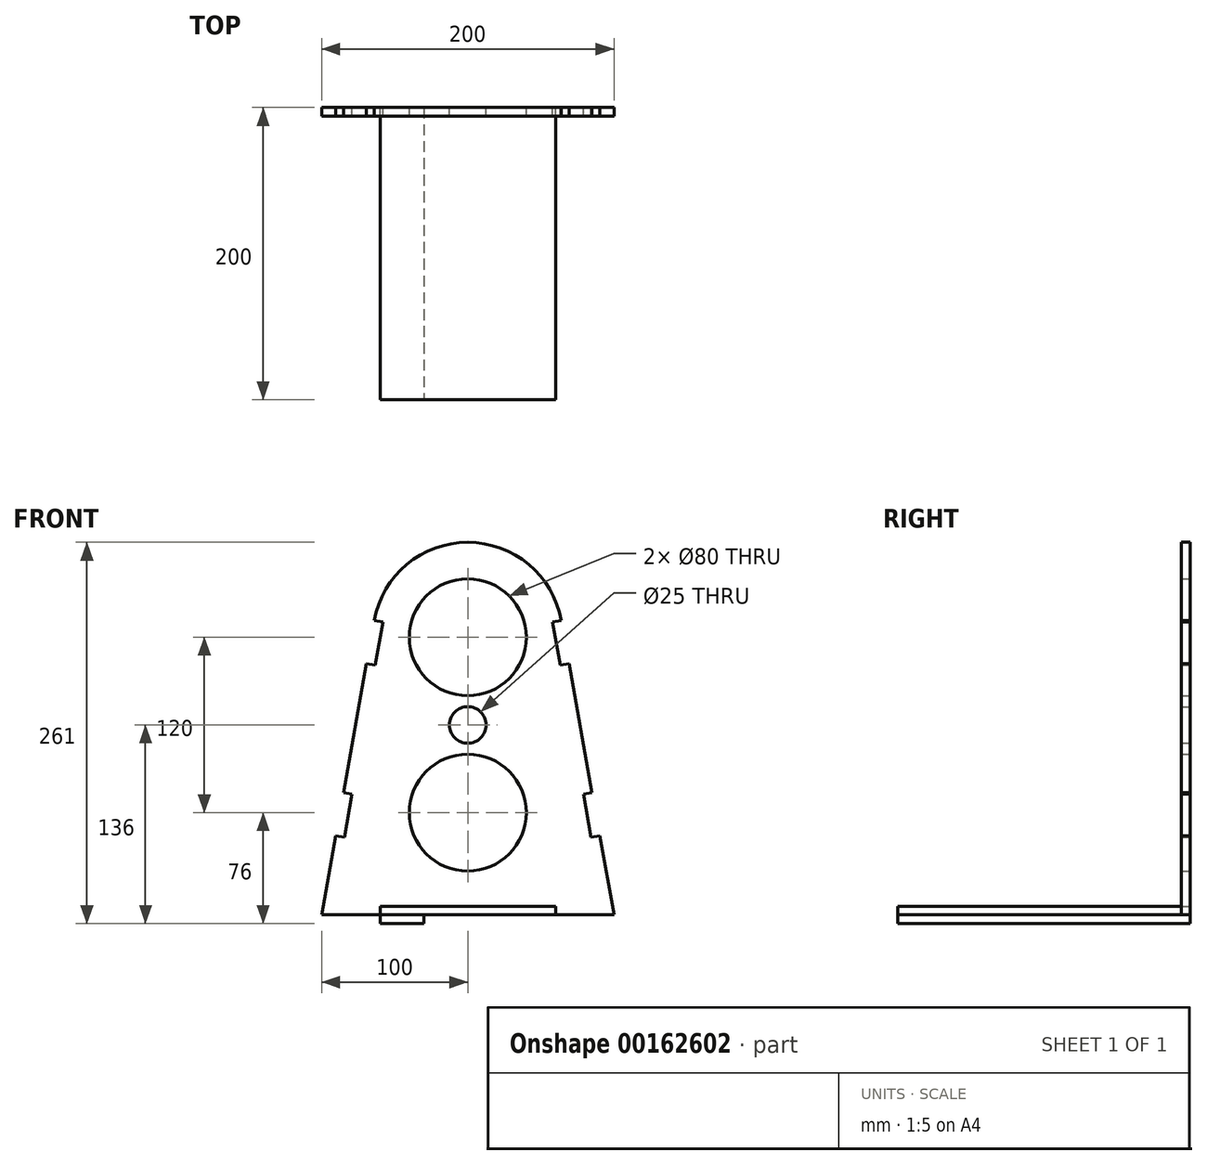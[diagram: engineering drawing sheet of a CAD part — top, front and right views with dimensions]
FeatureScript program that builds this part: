
annotation { "Feature Type Name" : "Feature", "Feature Type Description" : "" }
export const myFeature = defineFeature(function(context is Context, id is Id, definition is map)
    precondition{}
    {
        {
            var Q0;
            Q0=qCreatedBy(makeId("Front.planeOp"),FACE);
            var sketch = newSketch(context, id + "F0", { "sketchPlane" : qUnion([Q0])});
            skCircle(sketch, "E0", {"center": v(0, 0) * mm, "radius": 40 * mm});
            skLineSegment(sketch, "E1", {"start": v(0, 0) * mm, "end": v(0, 120) * mm, "construction": true});
            skCircle(sketch, "E2", {"center": v(0, 120) * mm, "radius": 40 * mm});
            skLineSegment(sketch, "E3", {"start": v(-100, -70) * mm, "end": v(-60, -70) * mm});
            skPoint(sketch, "E4", {"position": v(0, -70) * mm});
            skCircle(sketch, "E5", {"center": v(0, 60) * mm, "radius": 12.5 * mm});
            skArc(sketch, "E6", {"start": v(63.99, 131.44) * mm, "mid": v(0, 185) * mm, "end": v(-63.99, 131.44) * mm});
            skLineSegment(sketch, "E7", {"start": v(-100, -70) * mm, "end": v(-90.32, -15.86) * mm});
            skLineSegment(sketch, "E8", {"start": v(100, -70) * mm, "end": v(90.32, -15.86) * mm});
            skLineSegment(sketch, "E9", {"start": v(-63.99, 131.44) * mm, "end": v(-58.08, 130.38) * mm});
            skLineSegment(sketch, "E10", {"start": v(-58.08, 130.38) * mm, "end": v(-63.36, 100.85) * mm});
            skLineSegment(sketch, "E11", {"start": v(-63.36, 100.85) * mm, "end": v(-69.27, 101.9) * mm});
            skLineSegment(sketch, "E12", {"start": v(-85.04, 13.67) * mm, "end": v(-79.13, 12.62) * mm});
            skLineSegment(sketch, "E13", {"start": v(-79.13, 12.62) * mm, "end": v(-84.41, -16.91) * mm});
            skLineSegment(sketch, "E14", {"start": v(-84.41, -16.91) * mm, "end": v(-90.32, -15.86) * mm});
            skLineSegment(sketch, "E15.trimOffspring", {"start": v(-85.04, 13.67) * mm, "end": v(-69.27, 101.9) * mm});
            skLineSegment(sketch, "E16.MirrorCS", {"start": v(84.41, -16.91) * mm, "end": v(90.32, -15.86) * mm});
            skLineSegment(sketch, "E17.MirrorCS", {"start": v(79.13, 12.62) * mm, "end": v(84.41, -16.91) * mm});
            skLineSegment(sketch, "E18.MirrorCS", {"start": v(85.04, 13.67) * mm, "end": v(79.13, 12.62) * mm});
            skLineSegment(sketch, "E19.MirrorCS", {"start": v(63.99, 131.44) * mm, "end": v(58.08, 130.38) * mm});
            skLineSegment(sketch, "E20.MirrorCS", {"start": v(58.08, 130.38) * mm, "end": v(63.36, 100.85) * mm});
            skLineSegment(sketch, "E21.MirrorCS", {"start": v(63.36, 100.85) * mm, "end": v(69.27, 101.9) * mm});
            skLineSegment(sketch, "E22.trimOffspring", {"start": v(85.04, 13.67) * mm, "end": v(69.27, 101.9) * mm});
            skLineSegment(sketch, "E23", {"start": v(-60, -70) * mm, "end": v(-60, -64) * mm});
            skLineSegment(sketch, "E24", {"start": v(-60, -64) * mm, "end": v(0, -64) * mm});
            skLineSegment(sketch, "E25.MirrorCS", {"start": v(60, -64) * mm, "end": v(0, -64) * mm});
            skLineSegment(sketch, "E26.MirrorCS", {"start": v(60, -70) * mm, "end": v(60, -64) * mm});
            skLineSegment(sketch, "E27.trimOffspring", {"start": v(60, -70) * mm, "end": v(100, -70) * mm});
            skSolve(sketch);
        }
        {
            var Q0;
            Q0=qSketchRegion(id+"F0",true);
            extrude(context, id + "F1", {"entities" : qUnion([Q0]), "depth" : 6 * mm});
        }
        {
            var Q0;
            Q0=makeQuery(id+"F1.opExtrude","SWEPT_FACE",FACE,{"disambiguationData":[OSD([sQuery(id+"F0.wireOp",EDGE,"E24"),sQuery(id+"F0.wireOp",EDGE,"E25.MirrorCS")])]});
            var sketch = newSketch(context, id + "F2", { "sketchPlane" : qUnion([Q0])});
            skLineSegment(sketch, "E28.bottom", {"start": v(-60, 0) * mm, "end": v(60, 0) * mm});
            skLineSegment(sketch, "E28.top", {"start": v(-60, 200) * mm, "end": v(60, 200) * mm});
            skLineSegment(sketch, "E28.left", {"start": v(-60, 0) * mm, "end": v(-60, 200) * mm});
            skLineSegment(sketch, "E28.right", {"start": v(60, 0) * mm, "end": v(60, 200) * mm});
            skSolve(sketch);
        }
        {
            var Q0;
            Q0=qSketchRegion(id+"F2",true);
            extrude(context, id + "F3", {"entities" : qUnion([Q0]), "depth" : 6 * mm});
        }
        {
            var Q0;
            Q0=makeQuery(id+"F3.opExtrude","CAP_FACE",FACE,{"disambiguationData":[OSD([sQuery(id+"F2.wireOp",EDGE,"E28.top"),sQuery(id+"F2.wireOp",EDGE,"E28.left"),sQuery(id+"F2.wireOp",EDGE,"E28.right"),sQuery(id+"F2.wireOp",EDGE,"E28.bottom")])],"isStart":false});
            var sketch = newSketch(context, id + "F4", { "sketchPlane" : qUnion([Q0])});
            skLineSegment(sketch, "E29.bottom", {"start": v(-60, 0) * mm, "end": v(-30, 0) * mm});
            skLineSegment(sketch, "E29.top", {"start": v(-60, 200) * mm, "end": v(-30, 200) * mm});
            skLineSegment(sketch, "E29.left", {"start": v(-60, 0) * mm, "end": v(-60, 200) * mm});
            skLineSegment(sketch, "E29.right", {"start": v(-30, 0) * mm, "end": v(-30, 200) * mm});
            skSolve(sketch);
        }
        {
            var Q0;
            Q0=qSketchRegion(id+"F4",true);
            extrude(context, id + "F5", {"entities" : qUnion([Q0]), "depth" : 6 * mm});
        }
    });
